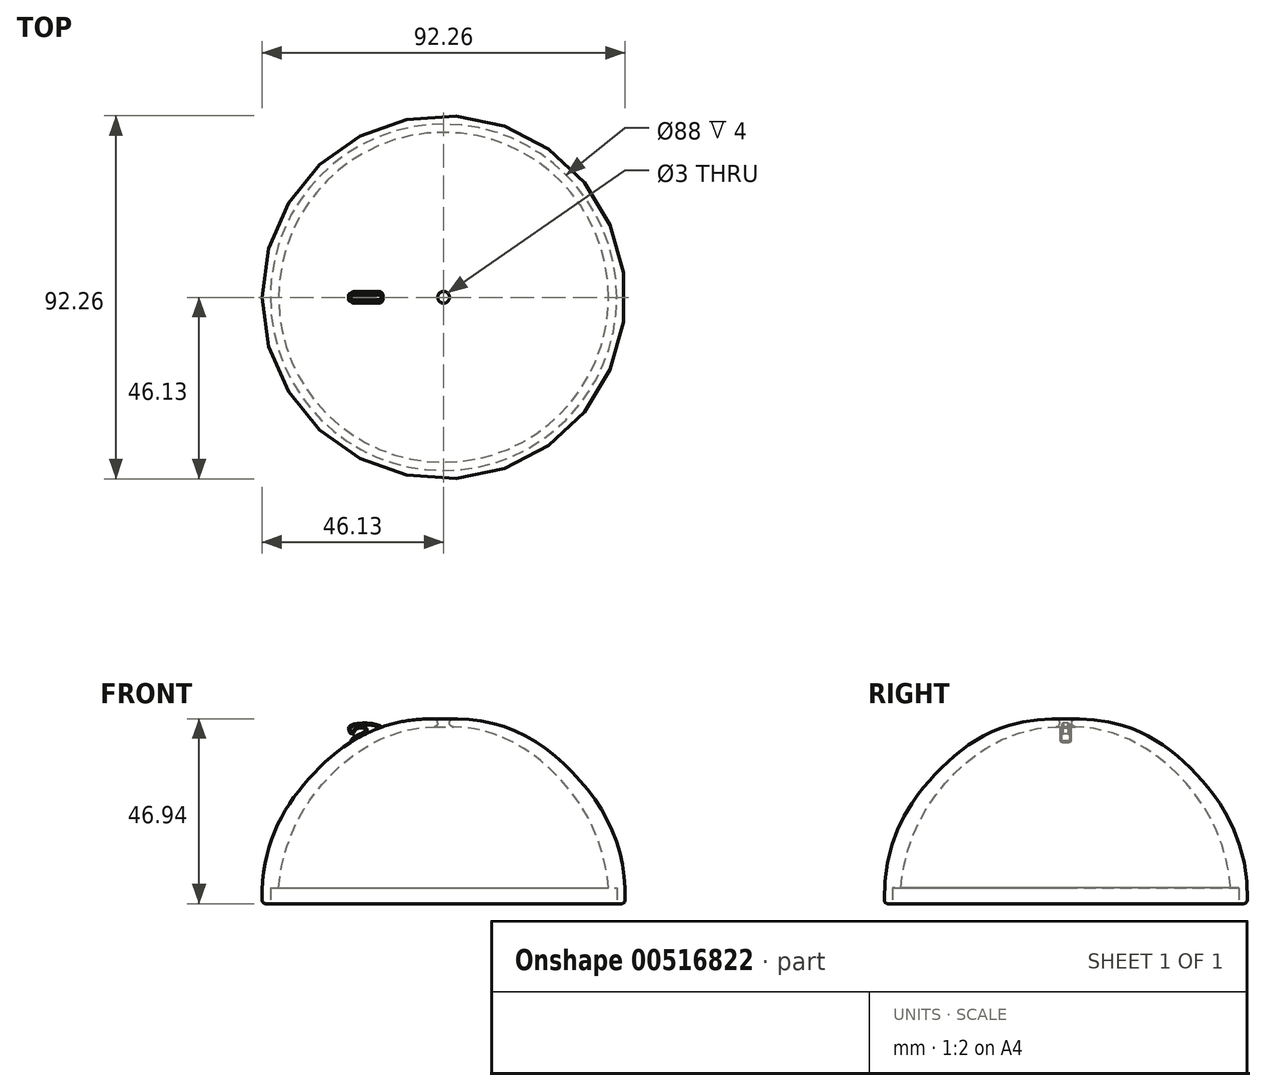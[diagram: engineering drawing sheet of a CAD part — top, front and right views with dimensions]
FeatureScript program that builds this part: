
annotation { "Feature Type Name" : "Feature", "Feature Type Description" : "" }
export const myFeature = defineFeature(function(context is Context, id is Id, definition is map)
    precondition{}
    {
        {
            var Q0;
            Q0=qCreatedBy(makeId("Front.planeOp"),FACE);
            var sketch = newSketch(context, id + "F0", { "sketchPlane" : qUnion([Q0])});
            skLineSegment(sketch, "E0", {"start": v(0, 0) * mm, "end": v(0, 45) * mm, "construction": true});
            skLineSegment(sketch, "E1", {"start": v(0, 0) * mm, "end": v(0, -45) * mm, "construction": true});
            skLineSegment(sketch, "E2", {"start": v(0, 0) * mm, "end": v(-45, 0) * mm, "construction": true});
            skSolve(sketch);
        }
        {
            var Q0;
            Q0=qCreatedBy(makeId("Front.planeOp"),FACE);
            var sketch = newSketch(context, id + "F1", { "sketchPlane" : qUnion([Q0])});
            skLineSegment(sketch, "E3", {"start": v(-46.1, 0) * mm, "end": v(-44, 0) * mm});
            skLineSegment(sketch, "E4", {"start": v(-44, 0) * mm, "end": v(-44, 4) * mm});
            skLineSegment(sketch, "E5", {"start": v(-44, 4) * mm, "end": v(-41.9, 4) * mm});
            skLineSegment(sketch, "E6", {"start": v(0, 44.94) * mm, "end": v(-1.5, 44.94) * mm, "construction": true});
            skFitSpline(sketch, "E7", {"points": [v(-41.9, 4) * mm, v(-29.99, 31.28) * mm, v(-1.5, 44.94) * mm], "startDerivative": vector(6.04, 66.31) * mm, "endDerivative": vector(69.52, -0.8) * mm});
            skLineSegment(sketch, "E8", {"start": v(-1.5, 44.94) * mm, "end": v(-1.5, 46.94) * mm});
            skLineSegment(sketch, "E9", {"start": v(-1.5, 46.94) * mm, "end": v(-3.5, 46.94) * mm});
            skFitSpline(sketch, "E10", {"points": [v(-3.5, 46.94) * mm, v(-34.22, 31.77) * mm, v(-46.1, 0) * mm], "startDerivative": vector(-82.6, -0.7) * mm, "endDerivative": vector(2.7, -83.57) * mm});
            skSolve(sketch);
        }
        {
            var Q0;
            Q0 = qSketchRegion(id + "F1", true);
            var Q1;
            Q1=sQuery(id+"F0.wireOp",EDGE,"E0");
            revolve(context, id + "F2", {"entities" : qUnion([Q0]), "axis" : qUnion([Q1]), "revolveType" : RevolveType.FULL});
        }
        {
            var Q0;
            Q0=makeQuery(id+"F2.opRevolve","SWEPT_EDGE",EDGE,{"disambiguationData":[OSD([sQuery(id+"F1.wireOp",EDGE,"E8"),sQuery(id+"F1.wireOp",EDGE,"E9")])]});
            var Q1;
            Q1=makeQuery(id+"F2.opRevolve","SWEPT_EDGE",EDGE,{"disambiguationData":[OSD([sQuery(id+"F1.wireOp",EDGE,"E7"),sQuery(id+"F1.wireOp",EDGE,"E8")])]});
            fillet(context, id + "F3", {"entities" : qUnion([Q0, Q1]), "radius" : 1 * mm, "tangentPropagation" : true, "allowEdgeOverflow" : false});
        }
        {
            var Q0;
            Q0=makeQuery(id+"F2.opRevolve","SWEPT_EDGE",EDGE,{"disambiguationData":[OSD([sQuery(id+"F1.wireOp",EDGE,"E3"),sQuery(id+"F1.wireOp",EDGE,"E10")])]});
            fillet(context, id + "F4", {"entities" : qUnion([Q0]), "radius" : 1 * mm, "tangentPropagation" : true, "allowEdgeOverflow" : false});
        }
        {
            var Q0;
            Q0=qCreatedBy(makeId("Front.planeOp"),FACE);
            var sketch = newSketch(context, id + "F5", { "sketchPlane" : qUnion([Q0])});
            skFitSpline(sketch, "E11", {"points": [v(-15.71, 44.83) * mm, v(-17.79, 45.7) * mm, v(-20.63, 45.88) * mm, v(-23.66, 45.28) * mm, v(-24.1, 44.35) * mm, v(-23.65, 43.3) * mm, v(-23.05, 43.15) * mm, v(-22.67, 43.62) * mm, v(-22.14, 44.35) * mm, v(-20.4, 44.64) * mm, v(-19.85, 44.21) * mm, v(-20.14, 43.7) * mm, v(-21.3, 43.12) * mm, v(-23.15, 42.04) * mm, v(-23.49, 41.03) * mm], "startDerivative": vector(-11.93, 17.1) * mm, "endDerivative": vector(-1.6, -15.9) * mm});
            skFitSpline(sketch, "E12", {"points": [v(-23.49, 41.03) * mm, v(-15.71, 44.83) * mm], "startDerivative": vector(7.77, 3.8) * mm, "endDerivative": vector(7.77, 3.8) * mm});
            skSolve(sketch);
        }
        {
            var Q0;
            Q0 = qSketchRegion(id + "F5", true);
            extrude(context, id + "F6", {"entities" : qUnion([Q0]), "operationType" : NewBodyOperationType.ADD, "endBound" : BoundingType.SYMMETRIC, "depth" : 2 * mm, "offsetDistance" : 25 * mm});
        }
        {
            var Q0;
            Q0=makeQuery(id+"F6.opExtrude","CAP_EDGE",EDGE,{"disambiguationData":[OSD([sQuery(id+"F5.wireOp",EDGE,"E11")])],"isStart":false});
            var Q1;
            Q1=makeQuery(id+"F6.opExtrude","CAP_EDGE",EDGE,{"disambiguationData":[OSD([sQuery(id+"F5.wireOp",EDGE,"E11")])],"isStart":true});
            var Q2;
            {var subQ0=sQuery(id+"F5.wireOp",EDGE,"E12");var subQ1=sQuery(id+"F5.wireOp",EDGE,"E11");Q2=makeQuery(id+"F6.opExtrude","SWEPT_EDGE",EDGE,{"disambiguationData":[OSD([subQ1,subQ0]),TDD([makeQuery(id+"F5.imprint","INTERSECT",VERTEX,{"disambiguationData":[OD(0.0)],"derivedFrom":[subQ1,subQ0]})])]});}
            fillet(context, id + "F7", {"entities" : qUnion([Q0, Q1, Q2]), "radius" : .4 * mm, "tangentPropagation" : true, "allowEdgeOverflow" : false});
        }
        {
            var Q0;
            Q0=makeQuery(id+"F6.boolean.opBoolean","INTERSECT",EDGE,{"derivedFrom":[makeQuery(id+"F2.opRevolve","SWEPT_FACE",FACE,{"disambiguationData":[OSD([sQuery(id+"F1.wireOp",EDGE,"E10")])]}),makeQuery(id+"F6.opExtrude","CAP_FACE",FACE,{"disambiguationData":[OSD([sQuery(id+"F5.wireOp",EDGE,"E11"),sQuery(id+"F5.wireOp",EDGE,"E12")])],"isStart":false})]});
            fillet(context, id + "F8", {"entities" : qUnion([Q0]), "radius" : .5 * mm, "tangentPropagation" : true, "allowEdgeOverflow" : false});
        }
    });
